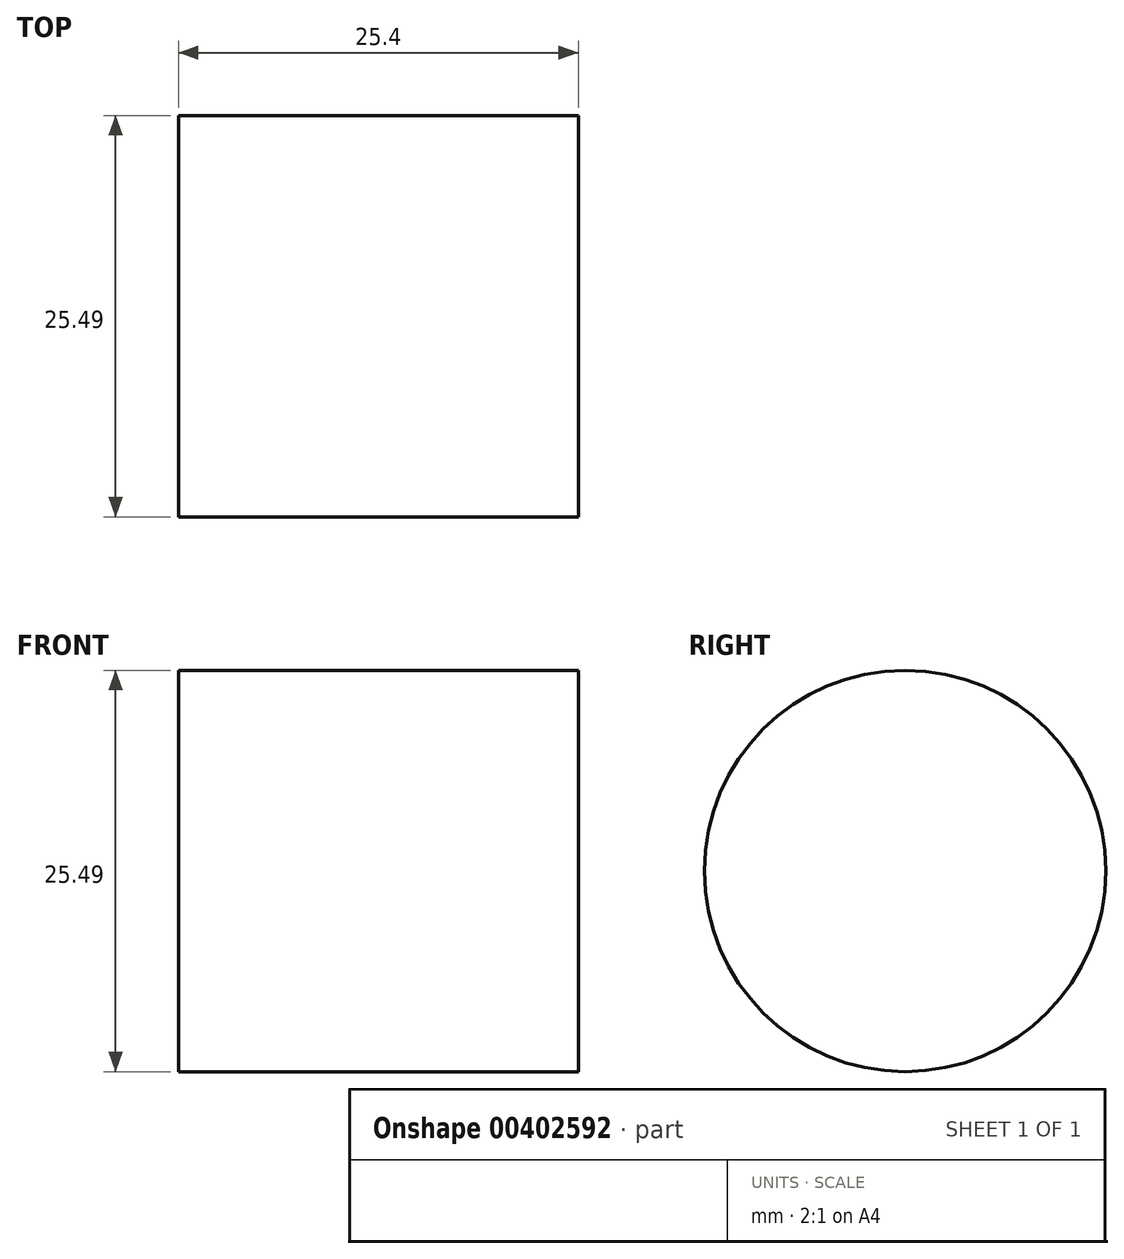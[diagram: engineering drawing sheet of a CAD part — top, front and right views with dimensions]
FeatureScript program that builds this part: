
annotation { "Feature Type Name" : "Feature", "Feature Type Description" : "" }
export const myFeature = defineFeature(function(context is Context, id is Id, definition is map)
    precondition{}
    {
        {
            var Q0;
            Q0=qCreatedBy(makeId("Right.planeOp"),FACE);
            var sketch = newSketch(context, id + "F0", { "sketchPlane" : qUnion([Q0])});
            skCircle(sketch, "E0", {"center": v(-39.85, -10.36) * mm, "radius": 12.75 * mm});
            skSolve(sketch);
        }
        {
            var Q0;
            Q0 = qSketchRegion(id + "F0", true);
            extrude(context, id + "F1", {"entities" : qUnion([Q0]), "depth" : 25.4 * mm});
        }
    });
